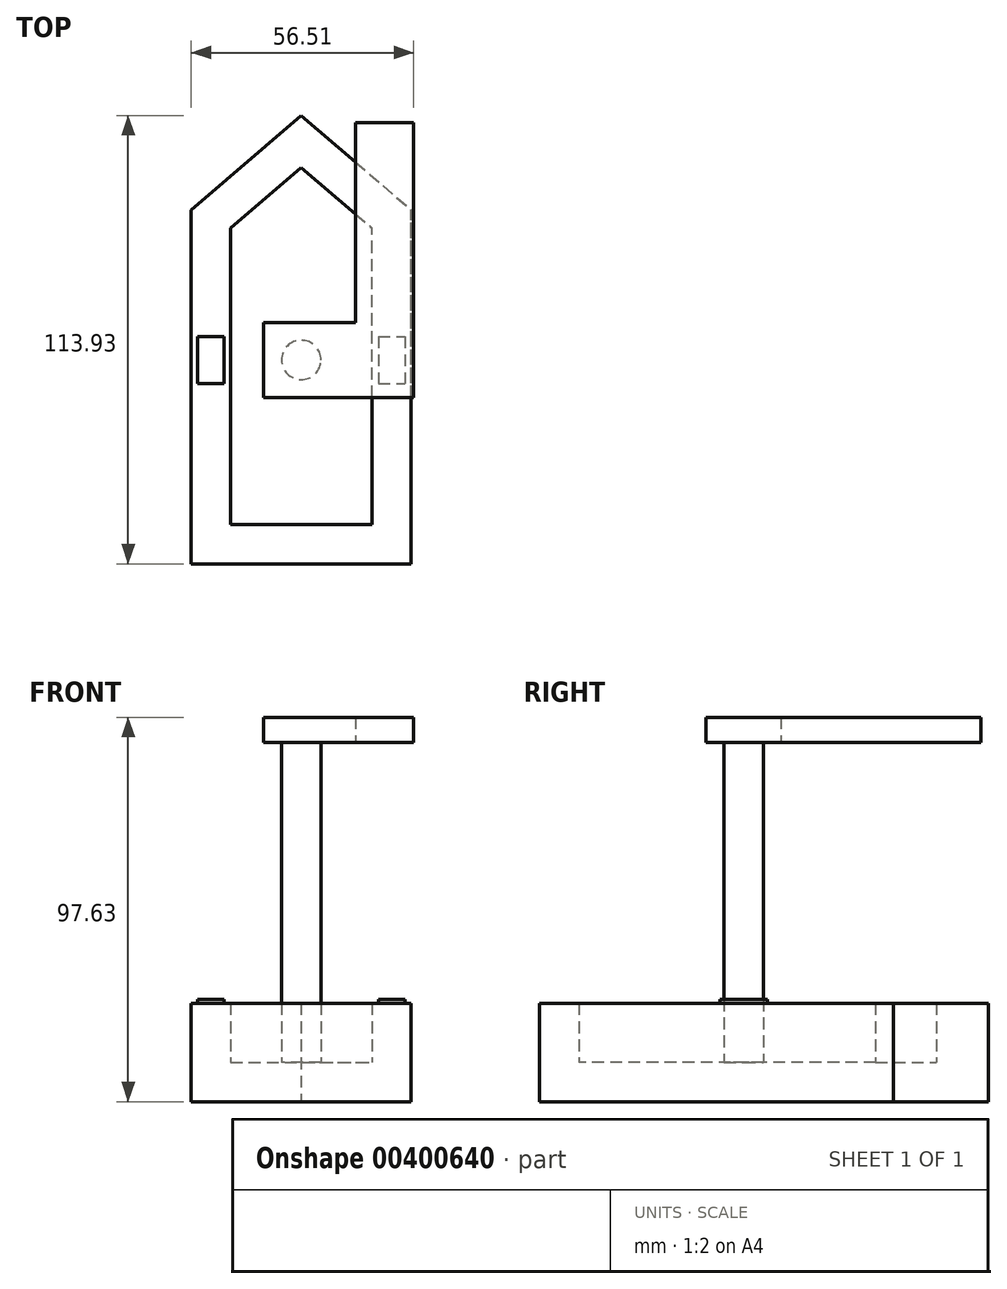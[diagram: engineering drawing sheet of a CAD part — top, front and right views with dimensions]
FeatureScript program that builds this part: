
annotation { "Feature Type Name" : "Feature", "Feature Type Description" : "" }
export const myFeature = defineFeature(function(context is Context, id is Id, definition is map)
    precondition{}
    {
        {
            var Q0;
            Q0=qCreatedBy(makeId("Top.planeOp"),FACE);
            var sketch = newSketch(context, id + "F0", { "sketchPlane" : qUnion([Q0])});
            skLineSegment(sketch, "E0.bottom", {"start": v(-27.94, 38.1) * mm, "end": v(27.94, 38.1) * mm});
            skLineSegment(sketch, "E0.top", {"start": v(-27.94, -38.1) * mm, "end": v(27.94, -38.1) * mm});
            skLineSegment(sketch, "E0.left", {"start": v(-27.94, 38.1) * mm, "end": v(-27.94, -38.1) * mm});
            skLineSegment(sketch, "E0.right", {"start": v(27.94, 38.1) * mm, "end": v(27.94, -38.1) * mm});
            skPoint(sketch, "E0.middle", {"position": v(0, 0) * mm});
            skPoint(sketch, "E1.end.orphan", {"position": v(0, 101.68) * mm});
            skLineSegment(sketch, "E2", {"start": v(-27.94, 38.1) * mm, "end": v(0, 62.11) * mm});
            skLineSegment(sketch, "E3", {"start": v(0, 62.11) * mm, "end": v(27.94, 38.1) * mm});
            skPoint(sketch, "E4.end.orphan", {"position": v(27.94, -43.76) * mm});
            skLineSegment(sketch, "E5", {"start": v(-27.94, -38.1) * mm, "end": v(-27.94, -51.82) * mm});
            skLineSegment(sketch, "E6", {"start": v(-27.94, -51.82) * mm, "end": v(27.94, -51.82) * mm});
            skLineSegment(sketch, "E7", {"start": v(27.94, -51.82) * mm, "end": v(27.94, -38.1) * mm});
            skSolve(sketch);
        }
        {
            var Q0;
            Q0 = qSketchRegion(id + "F0", true);
            extrude(context, id + "F1", {"entities" : qUnion([Q0]), "depth" : 25 * mm, "symmetric" : true});
        }
        {
            var Q0;
            Q0=makeQuery(id+"F1.opExtrude","CAP_FACE",FACE,{"disambiguationData":[OSD([sQuery(id+"F0.wireOp",EDGE,"E0.left"),sQuery(id+"F0.wireOp",EDGE,"E0.right"),sQuery(id+"F0.wireOp",EDGE,"E2"),sQuery(id+"F0.wireOp",EDGE,"E3"),sQuery(id+"F0.wireOp",EDGE,"E5"),sQuery(id+"F0.wireOp",EDGE,"E6"),sQuery(id+"F0.wireOp",EDGE,"E7")])],"isStart":false});
            shell(context, id + "F2", {"entities" : qUnion([Q0]), "thickness" : 10 * mm});
        }
        {
            var Q0;
            Q0=makeQuery(id+"F2.opShell","OFFSET_FACE",FACE,{"disambiguationData":[OSD([sQuery(id+"F0.wireOp",EDGE,"E0.left"),sQuery(id+"F0.wireOp",EDGE,"E0.right"),sQuery(id+"F0.wireOp",EDGE,"E2"),sQuery(id+"F0.wireOp",EDGE,"E3"),sQuery(id+"F0.wireOp",EDGE,"E5"),sQuery(id+"F0.wireOp",EDGE,"E6"),sQuery(id+"F0.wireOp",EDGE,"E7")])]});
            var sketch = newSketch(context, id + "F3", { "sketchPlane" : qUnion([Q0])});
            skCircle(sketch, "E8", {"center": v(0, 0) * mm, "radius": 5 * mm});
            skSolve(sketch);
        }
        {
            var Q0;
            Q0 = qSketchRegion(id + "F3", true);
            extrude(context, id + "F4", {"entities" : qUnion([Q0]), "operationType" : NewBodyOperationType.ADD, "depth" : 81.28 * mm});
        }
        {
            var Q0;
            Q0=makeQuery(id+"F1.opExtrude","CAP_FACE",FACE,{"disambiguationData":[OSD([sQuery(id+"F0.wireOp",EDGE,"E0.left"),sQuery(id+"F0.wireOp",EDGE,"E0.right"),sQuery(id+"F0.wireOp",EDGE,"E2"),sQuery(id+"F0.wireOp",EDGE,"E3"),sQuery(id+"F0.wireOp",EDGE,"E5"),sQuery(id+"F0.wireOp",EDGE,"E6"),sQuery(id+"F0.wireOp",EDGE,"E7")])],"isStart":false});
            var sketch = newSketch(context, id + "F5", { "sketchPlane" : qUnion([Q0])});
            skLineSegment(sketch, "E9.bottom", {"start": v(-19.6, 6) * mm, "end": v(-26.32, 6) * mm});
            skLineSegment(sketch, "E9.top", {"start": v(-19.6, -6) * mm, "end": v(-26.32, -6) * mm});
            skLineSegment(sketch, "E9.left", {"start": v(-19.6, 6) * mm, "end": v(-19.6, -6) * mm});
            skLineSegment(sketch, "E9.right", {"start": v(-26.32, 6) * mm, "end": v(-26.32, -6) * mm});
            skPoint(sketch, "E9.middle", {"position": v(-22.96, 0) * mm});
            skLineSegment(sketch, "E10.bottom", {"start": v(19.6, 6) * mm, "end": v(26.32, 6) * mm});
            skLineSegment(sketch, "E10.top", {"start": v(19.6, -6) * mm, "end": v(26.32, -6) * mm});
            skLineSegment(sketch, "E10.left", {"start": v(19.6, 6) * mm, "end": v(19.6, -6) * mm});
            skLineSegment(sketch, "E10.right", {"start": v(26.32, 6) * mm, "end": v(26.32, -6) * mm});
            skPoint(sketch, "E10.middle", {"position": v(22.96, 0) * mm});
            skSolve(sketch);
        }
        {
            var Q0;
            Q0 = qSketchRegion(id + "F5", true);
            extrude(context, id + "F6", {"entities" : qUnion([Q0]), "operationType" : NewBodyOperationType.ADD, "depth" : 1 * mm});
        }
        {
            var Q0;
            Q0=makeQuery(id+"F4.opExtrude","CAP_FACE",FACE,{"disambiguationData":[OSD([sQuery(id+"F3.wireOp",EDGE,"E8")])],"isStart":false});
            var sketch = newSketch(context, id + "F7", { "sketchPlane" : qUnion([Q0])});
            skLineSegment(sketch, "E11.bottom", {"start": v(9.53, -9.53) * mm, "end": v(-9.52, -9.53) * mm});
            skLineSegment(sketch, "E11.top", {"start": v(9.52, 9.53) * mm, "end": v(-9.53, 9.53) * mm});
            skLineSegment(sketch, "E11.left", {"start": v(9.53, -9.53) * mm, "end": v(9.52, 9.53) * mm});
            skLineSegment(sketch, "E11.right", {"start": v(-9.52, -9.53) * mm, "end": v(-9.53, 9.53) * mm});
            skPoint(sketch, "E11.middle", {"position": v(0, 0) * mm});
            skSolve(sketch);
        }
        {
            var Q0;
            Q0 = qSketchRegion(id + "F7", true);
            extrude(context, id + "F8", {"entities" : qUnion([Q0]), "operationType" : NewBodyOperationType.ADD, "depth" : 6.35 * mm});
        }
        {
            var Q0;
            Q0=makeQuery(id+"F8.opExtrude","SWEPT_FACE",FACE,{"disambiguationData":[OSD([sQuery(id+"F7.wireOp",EDGE,"E11.left")])]});
            var sketch = newSketch(context, id + "F9", { "sketchPlane" : qUnion([Q0])});
            skLineSegment(sketch, "E12.bottom", {"start": v(-9.53, 85.13) * mm, "end": v(9.53, 85.13) * mm});
            skLineSegment(sketch, "E12.top", {"start": v(-9.53, 78.78) * mm, "end": v(9.53, 78.78) * mm});
            skLineSegment(sketch, "E12.left", {"start": v(-9.53, 85.13) * mm, "end": v(-9.53, 78.78) * mm});
            skLineSegment(sketch, "E12.right", {"start": v(9.53, 85.13) * mm, "end": v(9.53, 78.78) * mm});
            skPoint(sketch, "E12.middle", {"position": v(0, 81.96) * mm});
            skSolve(sketch);
        }
        {
            var Q0;
            Q0 = qSketchRegion(id + "F9", true);
            extrude(context, id + "F10", {"entities" : qUnion([Q0]), "operationType" : NewBodyOperationType.ADD, "depth" : 19.05 * mm});
        }
        {
            var Q0;
            Q0=makeQuery(id+"F10.boolean.opBoolean","MERGE",FACE,{"derivedFrom":[makeQuery(id+"F8.opExtrude","SWEPT_FACE",FACE,{"disambiguationData":[OSD([sQuery(id+"F7.wireOp",EDGE,"E11.top")])]}),makeQuery(id+"F10.opExtrude","SWEPT_FACE",FACE,{"disambiguationData":[OSD([sQuery(id+"F9.wireOp",EDGE,"E12.right")])]})]});
            var sketch = newSketch(context, id + "F11", { "sketchPlane" : qUnion([Q0])});
            skLineSegment(sketch, "E13.bottom", {"start": v(-28.57, 85.13) * mm, "end": v(-13.8, 85.13) * mm});
            skLineSegment(sketch, "E13.top", {"start": v(-28.57, 78.78) * mm, "end": v(-13.8, 78.78) * mm});
            skLineSegment(sketch, "E13.left", {"start": v(-28.57, 85.13) * mm, "end": v(-28.57, 78.78) * mm});
            skLineSegment(sketch, "E13.right", {"start": v(-13.8, 85.13) * mm, "end": v(-13.8, 78.78) * mm});
            skPoint(sketch, "E13.middle", {"position": v(-21.18, 81.96) * mm});
            skSolve(sketch);
        }
        {
            var Q0;
            Q0 = qSketchRegion(id + "F11", true);
            extrude(context, id + "F12", {"entities" : qUnion([Q0]), "operationType" : NewBodyOperationType.ADD, "depth" : 50.8 * mm});
        }
    });
